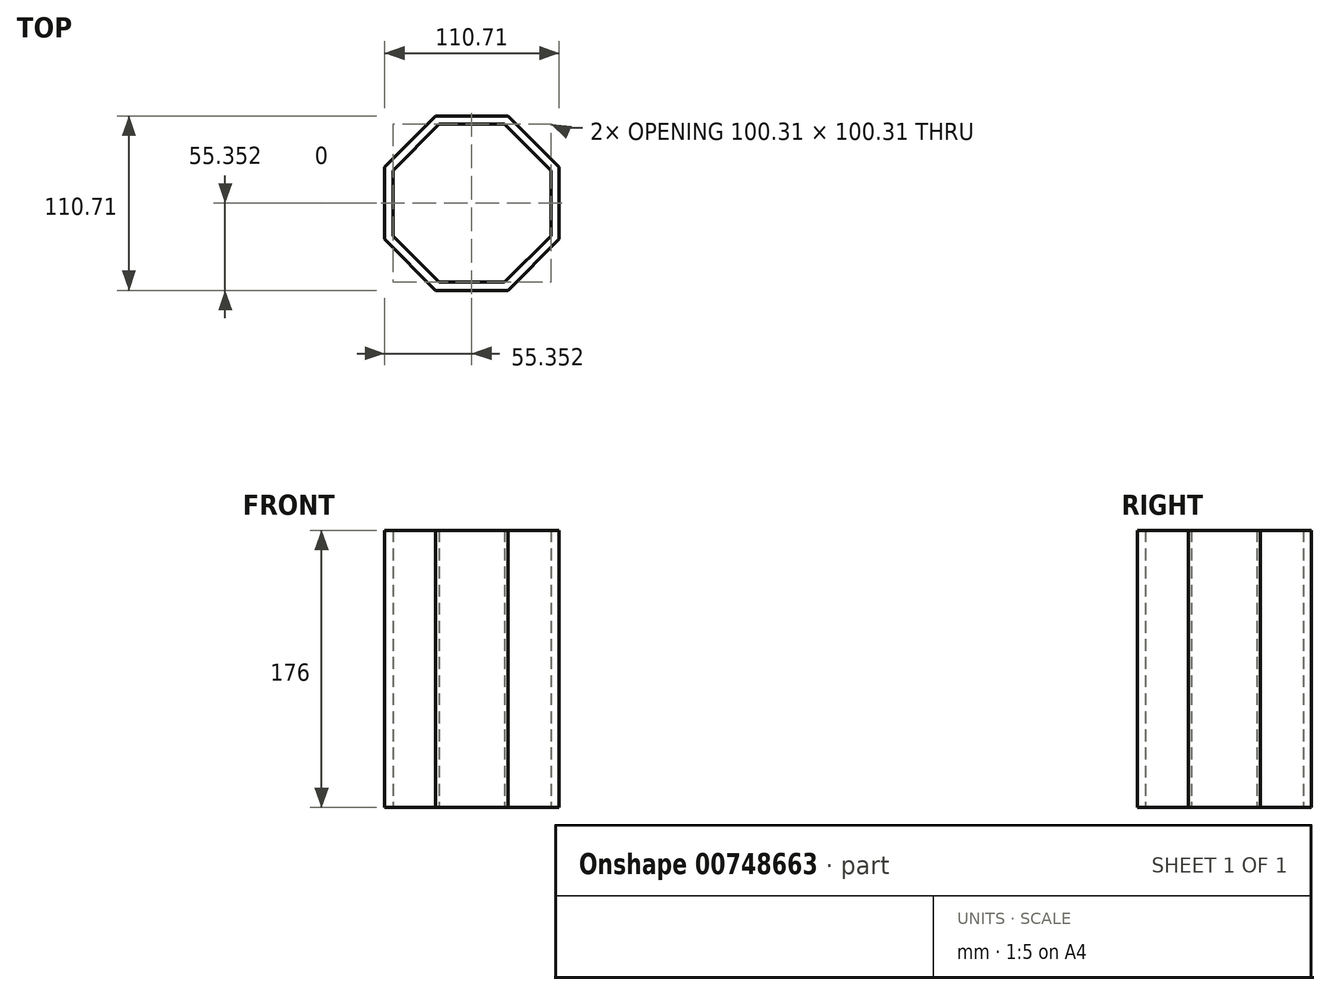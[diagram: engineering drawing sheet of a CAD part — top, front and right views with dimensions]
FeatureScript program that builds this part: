
annotation { "Feature Type Name" : "Feature", "Feature Type Description" : "" }
export const myFeature = defineFeature(function(context is Context, id is Id, definition is map)
    precondition{}
    {
        {
            var Q0;
            Q0=qCreatedBy(makeId("Top.planeOp"),FACE);
            var sketch = newSketch(context, id + "F0", { "sketchPlane" : qUnion([Q0])});
            skLineSegment(sketch, "E0.0", {"start": v(55.2, 22.78) * mm, "end": v(22.78, 55.2) * mm});
            skLineSegment(sketch, "E0.1", {"start": v(55.2, -23.08) * mm, "end": v(55.2, 22.78) * mm});
            skLineSegment(sketch, "E0.2", {"start": v(22.78, 55.2) * mm, "end": v(-23.08, 55.2) * mm});
            skLineSegment(sketch, "E0.3", {"start": v(22.78, -55.5) * mm, "end": v(55.2, -23.08) * mm});
            skLineSegment(sketch, "E0.4", {"start": v(-23.08, 55.2) * mm, "end": v(-55.5, 22.78) * mm});
            skLineSegment(sketch, "E0.5", {"start": v(-55.5, 22.78) * mm, "end": v(-55.5, -23.08) * mm});
            skLineSegment(sketch, "E0.6", {"start": v(-55.5, -23.08) * mm, "end": v(-23.08, -55.5) * mm});
            skLineSegment(sketch, "E0.7", {"start": v(-23.08, -55.5) * mm, "end": v(22.78, -55.5) * mm});
            skLineSegment(sketch, "E1.0", {"start": v(50, 20.63) * mm, "end": v(20.63, 50) * mm});
            skLineSegment(sketch, "E1.1", {"start": v(50, -20.92) * mm, "end": v(50, 20.63) * mm});
            skLineSegment(sketch, "E1.2", {"start": v(20.63, 50) * mm, "end": v(-20.92, 50) * mm});
            skLineSegment(sketch, "E1.3", {"start": v(20.63, -50.3) * mm, "end": v(50, -20.92) * mm});
            skLineSegment(sketch, "E1.4", {"start": v(-20.92, 50) * mm, "end": v(-50.3, 20.63) * mm});
            skLineSegment(sketch, "E1.5", {"start": v(-50.3, 20.63) * mm, "end": v(-50.3, -20.92) * mm});
            skLineSegment(sketch, "E1.6", {"start": v(-50.3, -20.92) * mm, "end": v(-20.92, -50.3) * mm});
            skLineSegment(sketch, "E1.7", {"start": v(-20.92, -50.3) * mm, "end": v(20.63, -50.3) * mm});
            skSolve(sketch);
        }
        {
            var Q0;
            Q0=makeQuery(id+"F0.imprint","IMPRINT",FACE,{"disambiguationData":[TD([[makeQuery(id+"F0.imprint","IMPRINT",EDGE,{"derivedFrom":sQuery(id+"F0.wireOp",EDGE,"E0.0")}),1.0]])]});
            extrude(context, id + "F1", {"entities" : qUnion([Q0]), "depth" : 176 * mm, "offsetDistance" : 25 * mm});
        }
    });
